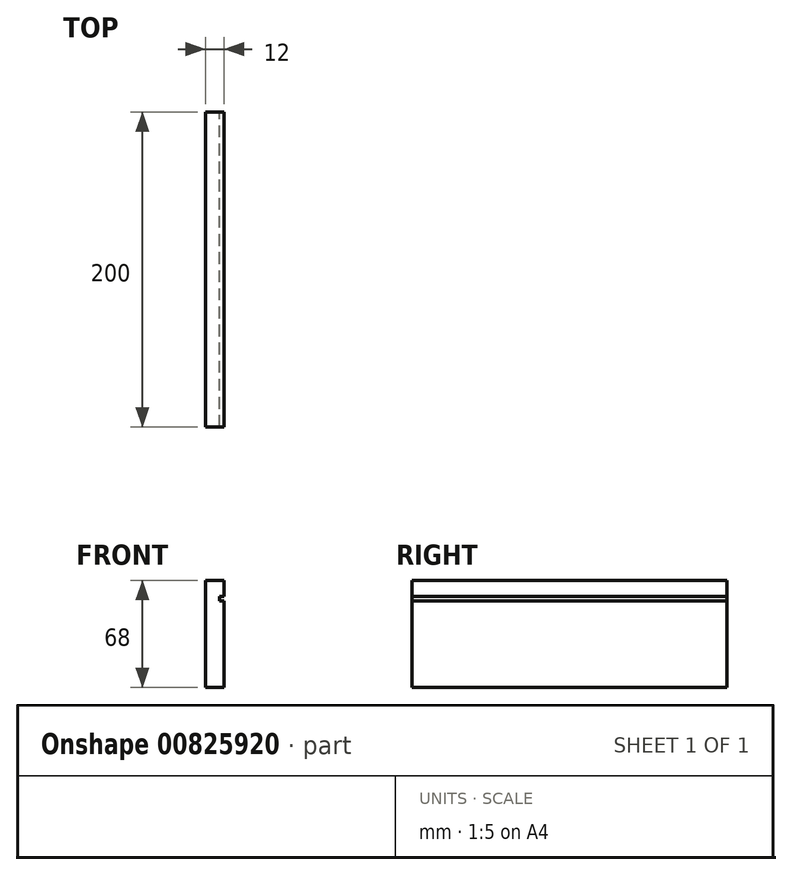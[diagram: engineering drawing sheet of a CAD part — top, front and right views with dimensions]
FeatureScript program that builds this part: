
annotation { "Feature Type Name" : "Feature", "Feature Type Description" : "" }
export const myFeature = defineFeature(function(context is Context, id is Id, definition is map)
    precondition{}
    {
        {
            var Q0;
            Q0=qCreatedBy(makeId("Front.planeOp"),FACE);
            var sketch = newSketch(context, id + "F0", { "sketchPlane" : qUnion([Q0])});
            skLineSegment(sketch, "E0.bottom", {"start": v(0, 68) * mm, "end": v(-12, 68) * mm});
            skLineSegment(sketch, "E0.top", {"start": v(0, 0) * mm, "end": v(-12, 0) * mm});
            skLineSegment(sketch, "E0.left", {"start": v(0, 68) * mm, "end": v(0, 58) * mm});
            skLineSegment(sketch, "E0.right", {"start": v(-12, 68) * mm, "end": v(-12, 0) * mm});
            skLineSegment(sketch, "E1.bottom", {"start": v(0, 58) * mm, "end": v(-3, 58) * mm});
            skLineSegment(sketch, "E1.top", {"start": v(0, 55) * mm, "end": v(-3, 55) * mm});
            skLineSegment(sketch, "E1.right", {"start": v(-3, 58) * mm, "end": v(-3, 55) * mm});
            skLineSegment(sketch, "E2.trimOffspring", {"start": v(0, 55) * mm, "end": v(0, 0) * mm});
            skSolve(sketch);
        }
        {
            var Q0;
            Q0 = qSketchRegion(id + "F0", true);
            extrude(context, id + "F1", {"entities" : qUnion([Q0]), "depth" : 200 * mm, "offsetDistance" : 25 * mm});
        }
    });
